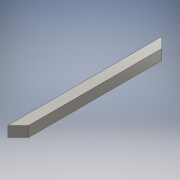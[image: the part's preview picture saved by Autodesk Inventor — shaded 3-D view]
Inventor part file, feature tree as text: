
AUTODESK INVENTOR PART (.ipt)
format: ipt  version: 2016 (Build 200138000, 138)  size: 108,544 bytes
history: native  units: mm
features: extrude x1, sketch x1
ambient origin geometry x8: Origin, YZ Plane, XZ Plane, XY Plane, X Axis, Y Axis, Z Axis, Center Point
bodies: Solid1 (feature_tree)
feature tree (2):
  extrude  "Extrusion1"  TaperAngle=45.0deg  [1 undecoded]
  sketch  "Sketch1"  dims[d2=45.0deg d3=45.0deg d4=140.0mm d5=0.0mm]
note: 1 required parameter value undecoded (feature->parameter linkage not recoverable at this tier; creation-order binding heuristic only, values carry confidence <= 0.55)
